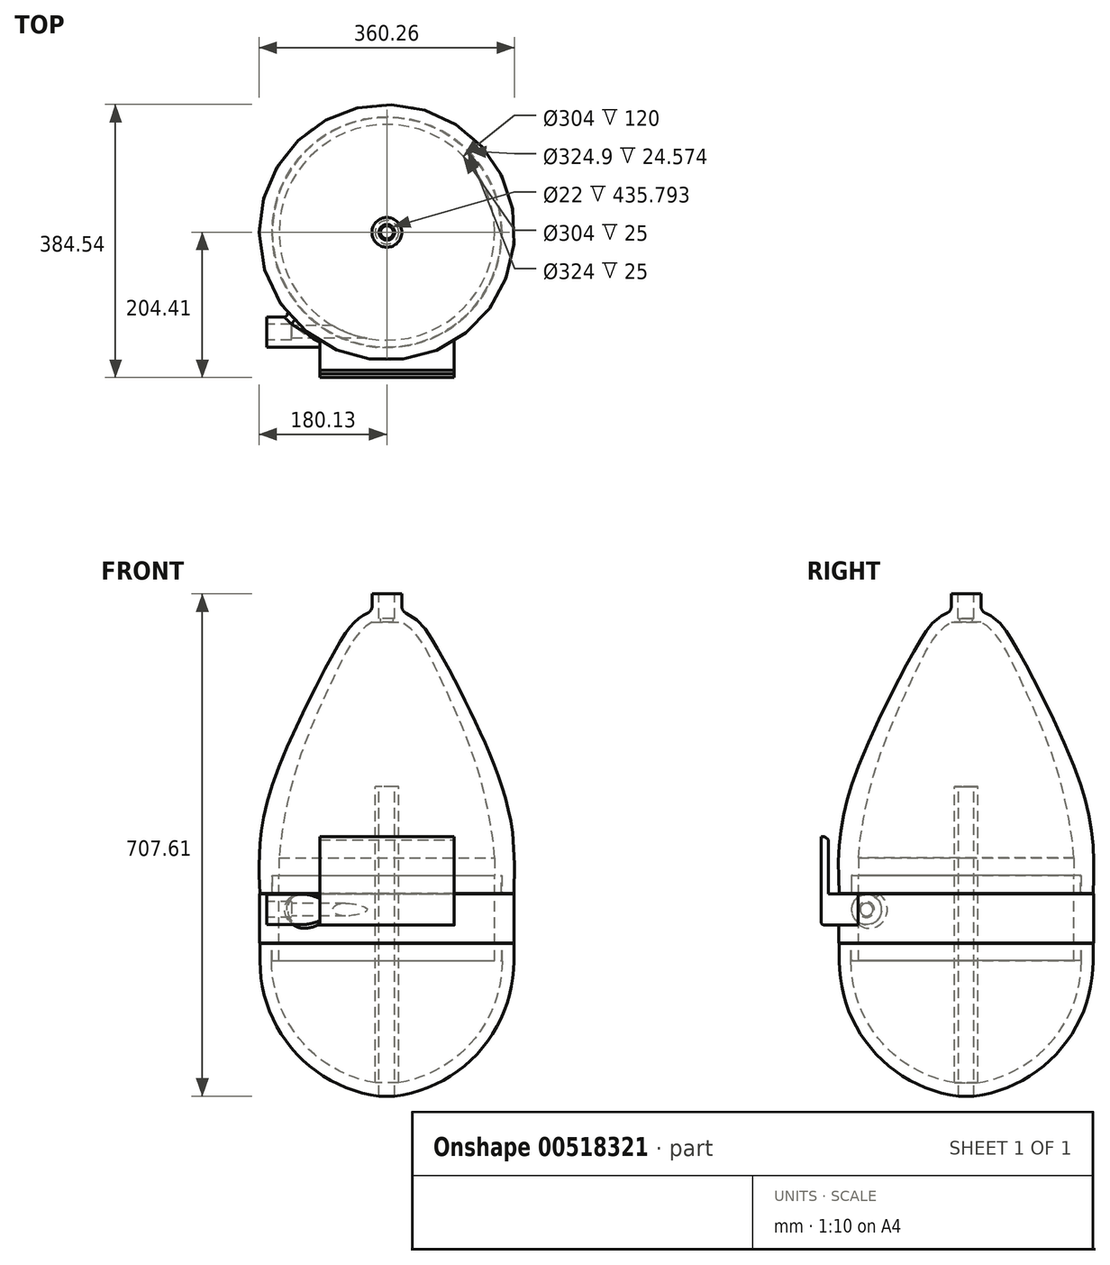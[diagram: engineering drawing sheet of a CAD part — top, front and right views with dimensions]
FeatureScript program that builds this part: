
annotation { "Feature Type Name" : "Feature", "Feature Type Description" : "" }
export const myFeature = defineFeature(function(context is Context, id is Id, definition is map)
    precondition{}
    {
        {
            var Q0;
            Q0=qCreatedBy(makeId("Front.planeOp"),FACE);
            var sketch = newSketch(context, id + "F0", { "sketchPlane" : qUnion([Q0])});
            skLineSegment(sketch, "E0", {"start": v(0, 331.82) * mm, "end": v(21, 331.82) * mm});
            skPoint(sketch, "E1", {"position": v(152, 0) * mm});
            skFitSpline(sketch, "E2", {"points": [v(21, 331.82) * mm, v(45.96, 308.45) * mm, v(72.3, 259.9) * mm, v(103.82, 190.2) * mm, v(132.28, 109.63) * mm, v(152, 0) * mm], "startDerivative": vector(216.06, -113.53) * mm, "endDerivative": vector(26.34, -404.99) * mm});
            skLineSegment(sketch, "E3", {"start": v(152, 0) * mm, "end": v(152, -50) * mm});
            skLineSegment(sketch, "E4", {"start": v(0, 0) * mm, "end": v(0, 359.59) * mm});
            skPoint(sketch, "E5", {"position": v(0, 346.82) * mm});
            skPoint(sketch, "E6", {"position": v(21, 346.82) * mm});
            skLineSegment(sketch, "E7", {"start": v(0, 346.82) * mm, "end": v(21, 346.82) * mm});
            skLineSegment(sketch, "E8", {"start": v(0, 346.82) * mm, "end": v(0, 331.82) * mm});
            skFitSpline(sketch, "E9", {"points": [v(21, 346.82) * mm, v(31.07, 342.93) * mm, v(45.96, 331.82) * mm, v(65.29, 305.23) * mm, v(159, 109.63) * mm, v(179.94, 0) * mm, v(179.02, -50) * mm], "startDerivative": vector(130.74, -24.6) * mm, "endDerivative": vector(-14.62, -301.81) * mm});
            skLineSegment(sketch, "E10", {"start": v(179.02, -50) * mm, "end": v(152, -50) * mm});
            skPoint(sketch, "E11", {"position": v(55.32, 293.43) * mm});
            skSolve(sketch);
        }
        {
            var Q0;
            Q0=makeQuery(id+"F0.imprint","IMPRINT",FACE,{"disambiguationData":[TD([[makeQuery(id+"F0.imprint","IMPRINT",EDGE,{"derivedFrom":sQuery(id+"F0.wireOp",EDGE,"E0")}),1.0]])]});
            var Q1;
            Q1=sQuery(id+"F0.wireOp",EDGE,"E4");
            revolve(context, id + "F1", {"entities" : qUnion([Q0]), "axis" : qUnion([Q1]), "revolveType" : RevolveType.FULL});
        }
        {
            var Q0;
            Q0=makeQuery(id+"F1.opRevolve","SWEPT_FACE",FACE,{"disambiguationData":[OSD([sQuery(id+"F0.wireOp",EDGE,"E7")])]});
            var sketch = newSketch(context, id + "F2", { "sketchPlane" : qUnion([Q0])});
            skCircle(sketch, "E12", {"center": v(0, 0) * mm, "radius": 9 * mm});
            skSolve(sketch);
        }
        {
            var Q0;
            Q0 = qSketchRegion(id + "F2", true);
            extrude(context, id + "F3", {"entities" : qUnion([Q0]), "operationType" : NewBodyOperationType.REMOVE, "oppositeDirection" : true, "depth" : 17 * mm, "offsetDistance" : 25 * mm});
        }
        {
            var Q0;
            Q0=makeQuery(id+"F1.opRevolve","SWEPT_FACE",FACE,{"disambiguationData":[OSD([sQuery(id+"F0.wireOp",EDGE,"E7")])]});
            var sketch = newSketch(context, id + "F4", { "sketchPlane" : qUnion([Q0])});
            skCircle(sketch, "E13", {"center": v(0, 0) * mm, "radius": 11.1 * mm});
            skSolve(sketch);
        }
        {
            var Q0;
            Q0 = qSketchRegion(id + "F4", true);
            extrude(context, id + "F5", {"entities" : qUnion([Q0]), "operationType" : NewBodyOperationType.REMOVE, "oppositeDirection" : true, "depth" : 10 * mm, "offsetDistance" : 25 * mm});
        }
        {
            var Q0;
            Q0=makeQuery(id+"F1.opRevolve","SWEPT_FACE",FACE,{"disambiguationData":[OSD([sQuery(id+"F0.wireOp",EDGE,"E7")])]});
            var sketch = newSketch(context, id + "F6", { "sketchPlane" : qUnion([Q0])});
            skCircle(sketch, "E14", {"center": v(0, 0) * mm, "radius": 21 * mm});
            skPoint(sketch, "E14.first.point", {"position": v(-12.3, 17.02) * mm});
            skPoint(sketch, "E14.second.point", {"position": v(20.38, 5.06) * mm});
            skPoint(sketch, "E14.third.point", {"position": v(-6.2, -20.06) * mm});
            skCircle(sketch, "E15", {"center": v(0, 0) * mm, "radius": 11.1 * mm});
            skPoint(sketch, "E15.first.point", {"position": v(-5.48, 9.65) * mm});
            skPoint(sketch, "E15.second.point", {"position": v(10.92, 2) * mm});
            skPoint(sketch, "E15.third.point", {"position": v(-2.11, -10.9) * mm});
            skSolve(sketch);
        }
        {
            var Q0;
            Q0 = qSketchRegion(id + "F6", true);
            extrude(context, id + "F7", {"entities" : qUnion([Q0]), "operationType" : NewBodyOperationType.ADD, "depth" : 25 * mm, "offsetDistance" : 25 * mm});
        }
        {
            var Q0;
            Q0=makeQuery(id+"F7.boolean.opBoolean","MERGE",EDGE,{"derivedFrom":[makeQuery(id+"F1.opRevolve","SWEPT_EDGE",EDGE,{"disambiguationData":[OSD([sQuery(id+"F0.wireOp",EDGE,"E7"),sQuery(id+"F0.wireOp",EDGE,"E9")])]}),makeQuery(id+"F7.opExtrude","CAP_EDGE",EDGE,{"disambiguationData":[OSD([sQuery(id+"F6.wireOp",EDGE,"E14")])],"isStart":true})]});
            fillet(context, id + "F8", {"entities" : qUnion([Q0]), "radius" : 10 * mm, "tangentPropagation" : true, "allowEdgeOverflow" : false});
        }
        {
            var Q0;
            Q0=makeQuery(id+"F1.opRevolve","SWEPT_FACE",FACE,{"disambiguationData":[OSD([sQuery(id+"F0.wireOp",EDGE,"E10")])]});
            var sketch = newSketch(context, id + "F9", { "sketchPlane" : qUnion([Q0])});
            skCircle(sketch, "E16", {"center": v(0, 0) * mm, "radius": 152 * mm});
            skPoint(sketch, "E16.first.point", {"position": v(90.88, 121.84) * mm});
            skPoint(sketch, "E16.second.point", {"position": v(-140.93, -56.95) * mm});
            skPoint(sketch, "E16.third.point", {"position": v(89.1, -123.15) * mm});
            skCircle(sketch, "E17", {"center": v(0, 0) * mm, "radius": 162 * mm});
            skSolve(sketch);
        }
        {
            var Q0;
            Q0 = qSketchRegion(id + "F9", true);
            extrude(context, id + "F10", {"entities" : qUnion([Q0]), "operationType" : NewBodyOperationType.REMOVE, "oppositeDirection" : true, "depth" : 25 * mm, "offsetDistance" : 25 * mm});
        }
        {
            var Q0;
            Q0=makeQuery(id+"F10.boolean.opBoolean","COPY",FACE,{"derivedFrom":makeQuery(id+"F10.opExtrude","CAP_FACE",FACE,{"disambiguationData":[OSD([sQuery(id+"F9.wireOp",EDGE,"E16"),sQuery(id+"F9.wireOp",EDGE,"E17")])],"isStart":false})});
            var sketch = newSketch(context, id + "F11", { "sketchPlane" : qUnion([Q0])});
            skCircle(sketch, "E18", {"center": v(0, 0) * mm, "radius": 152 * mm});
            skPoint(sketch, "E18.first.point", {"position": v(118.86, -94.74) * mm});
            skPoint(sketch, "E18.second.point", {"position": v(-147.64, -36.14) * mm});
            skPoint(sketch, "E18.third.point", {"position": v(31.37, 148.73) * mm});
            skCircle(sketch, "E19", {"center": v(0, 0) * mm, "radius": 161.5 * mm});
            skSolve(sketch);
        }
        {
            var Q0;
            Q0 = qSketchRegion(id + "F11", true);
            extrude(context, id + "F12", {"entities" : qUnion([Q0]), "depth" : 26 * mm, "offsetDistance" : 25 * mm});
        }
        {
            var Q0;
            Q0=makeQuery(id+"F12.opExtrude","CAP_FACE",FACE,{"disambiguationData":[OSD([sQuery(id+"F11.wireOp",EDGE,"E18"),sQuery(id+"F11.wireOp",EDGE,"E19")])],"isStart":false});
            var sketch = newSketch(context, id + "F13", { "sketchPlane" : qUnion([Q0])});
            skCircle(sketch, "E20", {"center": v(0, 0) * mm, "radius": 152 * mm});
            skPoint(sketch, "E20.first.point", {"position": v(152, 0) * mm});
            skPoint(sketch, "E20.second.point", {"position": v(-49.02, -143.88) * mm});
            skPoint(sketch, "E20.third.point", {"position": v(-36.04, 147.67) * mm});
            skCircle(sketch, "E21", {"center": v(0, 0) * mm, "radius": 179.5 * mm});
            skSolve(sketch);
        }
        {
            var Q0;
            Q0 = qSketchRegion(id + "F13", true);
            extrude(context, id + "F14", {"entities" : qUnion([Q0]), "operationType" : NewBodyOperationType.ADD, "depth" : 44 * mm, "offsetDistance" : 25 * mm});
        }
        {
            var Q0;
            Q0=makeQuery(id+"F14.opExtrude","CAP_FACE",FACE,{"disambiguationData":[OSD([sQuery(id+"F13.wireOp",EDGE,"E20"),sQuery(id+"F13.wireOp",EDGE,"E21")])],"isStart":false});
            var sketch = newSketch(context, id + "F15", { "sketchPlane" : qUnion([Q0])});
            skLineSegment(sketch, "E22.bottom", {"start": v(95.04, 152.28) * mm, "end": v(-94.69, 152.28) * mm});
            skLineSegment(sketch, "E22.top", {"start": v(95.04, 194.41) * mm, "end": v(-94.69, 194.41) * mm});
            skLineSegment(sketch, "E22.left", {"start": v(95.04, 152.28) * mm, "end": v(95.04, 194.41) * mm});
            skLineSegment(sketch, "E22.right", {"start": v(-94.69, 152.28) * mm, "end": v(-94.69, 194.41) * mm});
            skSolve(sketch);
        }
        {
            var Q0;
            Q0 = qSketchRegion(id + "F15", true);
            extrude(context, id + "F16", {"entities" : qUnion([Q0]), "operationType" : NewBodyOperationType.ADD, "oppositeDirection" : true, "depth" : 44 * mm, "offsetDistance" : 25 * mm});
        }
        {
            var Q0;
            Q0=makeQuery(id+"F16.opExtrude","SWEPT_FACE",FACE,{"disambiguationData":[OSD([sQuery(id+"F15.wireOp",EDGE,"E22.right")])]});
            var sketch = newSketch(context, id + "F17", { "sketchPlane" : qUnion([Q0])});
            skCircle(sketch, "E23", {"center": v(140.5, -73) * mm, "radius": 21.27 * mm});
            skPoint(sketch, "E23.centerSnap0", {"position": v(152.5, -73) * mm});
            skSolve(sketch);
        }
        {
            var Q0;
            Q0 = qSketchRegion(id + "F17", true);
            extrude(context, id + "F18", {"entities" : qUnion([Q0]), "operationType" : NewBodyOperationType.ADD, "depth" : 75 * mm, "offsetDistance" : 25 * mm});
        }
        {
            var Q0;
            Q0=makeQuery(id+"F18.opExtrude","CAP_FACE",FACE,{"disambiguationData":[OSD([sQuery(id+"F17.wireOp",EDGE,"E23")])],"isStart":false});
            var sketch = newSketch(context, id + "F19", { "sketchPlane" : qUnion([Q0])});
            skCircle(sketch, "E24", {"center": v(140.5, -73) * mm, "radius": 9 * mm});
            skSolve(sketch);
        }
        {
            var Q0;
            Q0 = qSketchRegion(id + "F19", true);
            extrude(context, id + "F20", {"entities" : qUnion([Q0]), "operationType" : NewBodyOperationType.REMOVE, "oppositeDirection" : true, "depth" : 143 * mm, "offsetDistance" : 25 * mm});
        }
        {
            var Q0;
            Q0=makeQuery(id+"F16.boolean.opBoolean","MERGE",FACE,{"derivedFrom":[makeQuery(id+"F14.opExtrude","CAP_FACE",FACE,{"disambiguationData":[OSD([sQuery(id+"F13.wireOp",EDGE,"E20"),sQuery(id+"F13.wireOp",EDGE,"E21")])],"isStart":false}),makeQuery(id+"F16.opExtrude","CAP_FACE",FACE,{"disambiguationData":[OSD([sQuery(id+"F15.wireOp",EDGE,"E22.bottom"),sQuery(id+"F15.wireOp",EDGE,"E22.top"),sQuery(id+"F15.wireOp",EDGE,"E22.left"),sQuery(id+"F15.wireOp",EDGE,"E22.right")])],"isStart":true})]});
            var sketch = newSketch(context, id + "F21", { "sketchPlane" : qUnion([Q0])});
            skCircle(sketch, "E25", {"center": v(0, 0) * mm, "radius": 152 * mm});
            skPoint(sketch, "E25.first.point", {"position": v(105.1, 109.8) * mm});
            skPoint(sketch, "E25.second.point", {"position": v(-35.54, -147.79) * mm});
            skPoint(sketch, "E25.third.point", {"position": v(-116.2, 97.98) * mm});
            skCircle(sketch, "E26", {"center": v(0, 0) * mm, "radius": 179.5 * mm});
            skPoint(sketch, "E26.first.point", {"position": v(142, 109.8) * mm});
            skPoint(sketch, "E26.second.point", {"position": v(0.2, -179.5) * mm});
            skPoint(sketch, "E26.second.point.positionSnap0", {"position": v(-0.2, -179.5) * mm});
            skPoint(sketch, "E26.third.point", {"position": v(-173.72, 45.18) * mm});
            skSolve(sketch);
        }
        {
            var Q0;
            Q0 = qSketchRegion(id + "F21", true);
            extrude(context, id + "F22", {"entities" : qUnion([Q0]), "operationType" : NewBodyOperationType.ADD, "depth" : 25 * mm, "offsetDistance" : 25 * mm});
        }
        {
            var Q0;
            Q0=makeQuery(id+"F16.opExtrude","SWEPT_FACE",FACE,{"disambiguationData":[OSD([sQuery(id+"F15.wireOp",EDGE,"E22.top")])]});
            var sketch = newSketch(context, id + "F23", { "sketchPlane" : qUnion([Q0])});
            skLineSegment(sketch, "E27.bottom", {"start": v(95.04, -95) * mm, "end": v(-94.69, -95) * mm});
            skLineSegment(sketch, "E27.top", {"start": v(95.04, 55) * mm, "end": v(-94.69, 55) * mm});
            skLineSegment(sketch, "E27.left", {"start": v(95.04, -95) * mm, "end": v(95.04, 55) * mm});
            skLineSegment(sketch, "E27.right", {"start": v(-94.69, -95) * mm, "end": v(-94.69, 55) * mm});
            skSolve(sketch);
        }
        {
            var Q0;
            Q0 = qSketchRegion(id + "F23", true);
            extrude(context, id + "F24", {"entities" : qUnion([Q0]), "operationType" : NewBodyOperationType.ADD, "depth" : 10 * mm, "offsetDistance" : 25 * mm});
        }
        {
            var Q0;
            Q0=makeQuery(id+"F24.opExtrude","CAP_FACE",FACE,{"disambiguationData":[OSD([sQuery(id+"F23.wireOp",EDGE,"E27.bottom"),sQuery(id+"F23.wireOp",EDGE,"E27.top"),sQuery(id+"F23.wireOp",EDGE,"E27.left"),sQuery(id+"F23.wireOp",EDGE,"E27.right")])],"isStart":false});
            var sketch = newSketch(context, id + "F25", { "sketchPlane" : qUnion([Q0])});
            skLineSegment(sketch, "E28.bottom", {"start": v(-94.69, 55) * mm, "end": v(95.04, 55) * mm});
            skLineSegment(sketch, "E28.top", {"start": v(-94.69, 30) * mm, "end": v(95.04, 30) * mm});
            skLineSegment(sketch, "E28.left", {"start": v(-94.69, 55) * mm, "end": v(-94.69, 30) * mm});
            skLineSegment(sketch, "E28.right", {"start": v(95.04, 55) * mm, "end": v(95.04, 30) * mm});
            skSolve(sketch);
        }
        {
            var Q0;
            Q0 = qSketchRegion(id + "F25", true);
            extrude(context, id + "F26", {"entities" : qUnion([Q0]), "operationType" : NewBodyOperationType.REMOVE, "oppositeDirection" : true, "depth" : 15 * mm, "offsetDistance" : 25 * mm});
        }
        {
            var Q0;
            Q0=makeQuery(id+"F24.opExtrude","CAP_EDGE",EDGE,{"disambiguationData":[OSD([sQuery(id+"F23.wireOp",EDGE,"E27.bottom")])],"isStart":false});
            fillet(context, id + "F27", {"entities" : qUnion([Q0]), "radius" : 5 * mm, "tangentPropagation" : true, "allowEdgeOverflow" : false});
        }
        {
            var Q0;
            Q0=makeQuery(id+"F22.opExtrude","CAP_FACE",FACE,{"disambiguationData":[OSD([sQuery(id+"F21.wireOp",EDGE,"E25"),sQuery(id+"F21.wireOp",EDGE,"E26")])],"isStart":false});
            var sketch = newSketch(context, id + "F28", { "sketchPlane" : qUnion([Q0])});
            skCircle(sketch, "E29", {"center": v(0, 0) * mm, "radius": 152 * mm});
            skPoint(sketch, "E29.first.point", {"position": v(-42.08, 146.06) * mm});
            skPoint(sketch, "E29.second.point", {"position": v(144.39, -47.5) * mm});
            skPoint(sketch, "E29.third.point", {"position": v(-99.24, -115.13) * mm});
            skCircle(sketch, "E30", {"center": v(0, 0) * mm, "radius": 162 * mm});
            skSolve(sketch);
        }
        {
            var Q0;
            Q0 = qSketchRegion(id + "F28", true);
            extrude(context, id + "F29", {"entities" : qUnion([Q0]), "operationType" : NewBodyOperationType.ADD, "depth" : 25 * mm, "offsetDistance" : 25 * mm});
        }
        {
            var Q0;
            Q0=qCreatedBy(makeId("Right.planeOp"),FACE);
            var sketch = newSketch(context, id + "F30", { "sketchPlane" : qUnion([Q0])});
            skLineSegment(sketch, "E31", {"start": v(-162.45, -120.8) * mm, "end": v(-162.45, -145.37) * mm});
            skLineSegment(sketch, "E32", {"start": v(-162.45, -120.8) * mm, "end": v(-178.93, -120.8) * mm});
            skLineSegment(sketch, "E33", {"start": v(-178.93, -120.8) * mm, "end": v(-178.93, -145.37) * mm});
            skArc(sketch, "E34", {"start": v(-162.45, -145.37) * mm, "mid": v(-115.5, -264.21) * mm, "end": v(0, -318.87) * mm});
            skArc(sketch, "E35", {"start": v(-178.93, -145.37) * mm, "mid": v(-127.24, -276.41) * mm, "end": v(0, -336.86) * mm});
            skLineSegment(sketch, "E36", {"start": v(0, -336.86) * mm, "end": v(0, -318.87) * mm});
            skLineSegment(sketch, "E37", {"start": v(0, -154.91) * mm, "end": v(0, -349.77) * mm});
            skSolve(sketch);
        }
        {
            var Q0;
            Q0=makeQuery(id+"F30.imprint","IMPRINT",FACE,{"disambiguationData":[TD([[makeQuery(id+"F30.imprint","IMPRINT",EDGE,{"derivedFrom":sQuery(id+"F30.wireOp",EDGE,"E31")}),-1.0]])]});
            var Q1;
            Q1=sQuery(id+"F30.wireOp",EDGE,"E37");
            revolve(context, id + "F31", {"entities" : qUnion([Q0]), "axis" : qUnion([Q1]), "revolveType" : RevolveType.FULL});
        }
        {
            var Q0;
            Q0=qCreatedBy(makeId("Top.planeOp"),FACE);
            var sketch = newSketch(context, id + "F32", { "sketchPlane" : qUnion([Q0])});
            skCircle(sketch, "E38", {"center": v(0, 0) * mm, "radius": 16.5 * mm});
            skCircle(sketch, "E39", {"center": v(0, 0) * mm, "radius": 11 * mm});
            skSolve(sketch);
        }
        {
            var Q0;
            Q0 = qSketchRegion(id + "F32", true);
            extrude(context, id + "F33", {"entities" : qUnion([Q0]), "operationType" : NewBodyOperationType.ADD, "oppositeDirection" : true, "depth" : 335 * mm, "offsetDistance" : 25 * mm});
        }
        {
            var Q0;
            Q0=qCreatedBy(makeId("Top.planeOp"),FACE);
            var sketch = newSketch(context, id + "F34", { "sketchPlane" : qUnion([Q0])});
            skCircle(sketch, "E40", {"center": v(0, 0) * mm, "radius": 11 * mm});
            skSolve(sketch);
        }
        {
            var Q0;
            Q0 = qSketchRegion(id + "F34", true);
            extrude(context, id + "F35", {"entities" : qUnion([Q0]), "operationType" : NewBodyOperationType.REMOVE, "oppositeDirection" : true, "depth" : 338.6 * mm, "offsetDistance" : 25 * mm});
        }
        {
            var Q0;
            Q0=makeQuery(id+"F16.opExtrude","SWEPT_EDGE",EDGE,{"disambiguationData":[OSD([sQuery(id+"F13.wireOp",EDGE,"E21"),sQuery(id+"F15.wireOp",EDGE,"E22.bottom"),sQuery(id+"F15.wireOp",EDGE,"E22.left")])]});
            var Q1;
            {var subQ0=sQuery(id+"F15.wireOp",EDGE,"E22.right");var subQ1=makeQuery(id+"F16.opExtrude","SWEPT_FACE",FACE,{"disambiguationData":[OSD([subQ0])]});var subQ2=sQuery(id+"F13.wireOp",EDGE,"E21");var subQ3=makeQuery(id+"F14.opExtrude","SWEPT_FACE",FACE,{"disambiguationData":[OSD([subQ2])]});Q1=makeQuery(id+"F18.boolean.opBoolean","SPLIT",EDGE,{"disambiguationData":[TD([makeQuery(id+"F14.opExtrude","CAP_FACE",FACE,{"disambiguationData":[OSD([sQuery(id+"F13.wireOp",EDGE,"E20"),subQ2])],"isStart":false})])],"derivedFrom":makeQuery(id+"F16.boolean.opBoolean","INTERSECT",EDGE,{"derivedFrom":[subQ3,subQ1]})});}
            var Q2;
            Q2=makeQuery(id+"F18.boolean.opBoolean","INTERSECT",EDGE,{"derivedFrom":[makeQuery(id+"F14.opExtrude","SWEPT_FACE",FACE,{"disambiguationData":[OSD([sQuery(id+"F13.wireOp",EDGE,"E21")])]}),makeQuery(id+"F18.opExtrude","SWEPT_FACE",FACE,{"disambiguationData":[OSD([sQuery(id+"F17.wireOp",EDGE,"E23")])]})]});
            var Q3;
            Q3=makeQuery(id+"F18.opExtrude","CAP_EDGE",EDGE,{"disambiguationData":[OSD([sQuery(id+"F17.wireOp",EDGE,"E23")])],"isStart":true});
            var Q4;
            Q4=makeQuery(id+"F22.opExtrude","CAP_EDGE",EDGE,{"disambiguationData":[OSD([sQuery(id+"F21.wireOp",EDGE,"E26")])],"isStart":true});
            fillet(context, id + "F36", {"entities" : qUnion([Q0, Q1, Q2, Q3, Q4]), "radius" : 5 * mm, "tangentPropagation" : true, "allowEdgeOverflow" : false});
        }
        {
            var Q0;
            Q0=makeQuery(id+"F33.opExtrude","CAP_FACE",FACE,{"disambiguationData":[OSD([sQuery(id+"F32.wireOp",EDGE,"E38"),sQuery(id+"F32.wireOp",EDGE,"E39")])],"isStart":true});
            var sketch = newSketch(context, id + "F37", { "sketchPlane" : qUnion([Q0])});
            skCircle(sketch, "E41", {"center": v(0, 0) * mm, "radius": 11 * mm});
            skPoint(sketch, "E41.first.point", {"position": v(2.37, -10.74) * mm});
            skPoint(sketch, "E41.second.point", {"position": v(-9.82, 4.96) * mm});
            skPoint(sketch, "E41.third.point", {"position": v(8.52, 6.96) * mm});
            skCircle(sketch, "E42", {"center": v(0, 0) * mm, "radius": 16.5 * mm});
            skPoint(sketch, "E42.first.point", {"position": v(-9.98, -13.14) * mm});
            skPoint(sketch, "E42.second.point", {"position": v(15.35, -6.06) * mm});
            skPoint(sketch, "E42.third.point", {"position": v(-9.77, 13.3) * mm});
            skSolve(sketch);
        }
        {
            var Q0;
            Q0 = qSketchRegion(id + "F37", true);
            extrude(context, id + "F38", {"entities" : qUnion([Q0]), "operationType" : NewBodyOperationType.ADD, "depth" : 100 * mm, "offsetDistance" : 25 * mm});
        }
        {
            var Q0;
            Q0=makeQuery(id+"F26.boolean.opBoolean","COPY",EDGE,{"derivedFrom":makeQuery(id+"F26.opExtrude","SWEPT_EDGE",EDGE,{"disambiguationData":[OSD([sQuery(id+"F23.wireOp",EDGE,"E27.left"),sQuery(id+"F25.wireOp",EDGE,"E28.top"),sQuery(id+"F25.wireOp",EDGE,"E28.right")])]})});
            var Q1;
            Q1=makeQuery(id+"F26.boolean.opBoolean","INTERSECT",EDGE,{"derivedFrom":[makeQuery(id+"F24.opExtrude","CAP_FACE",FACE,{"disambiguationData":[OSD([sQuery(id+"F23.wireOp",EDGE,"E27.bottom"),sQuery(id+"F23.wireOp",EDGE,"E27.top"),sQuery(id+"F23.wireOp",EDGE,"E27.left"),sQuery(id+"F23.wireOp",EDGE,"E27.right")])],"isStart":true}),makeQuery(id+"F26.opExtrude","SWEPT_FACE",FACE,{"disambiguationData":[OSD([sQuery(id+"F25.wireOp",EDGE,"E28.top")])]})]});
            var Q2;
            Q2=makeQuery(id+"F26.boolean.opBoolean","COPY",EDGE,{"derivedFrom":makeQuery(id+"F26.opExtrude","SWEPT_EDGE",EDGE,{"disambiguationData":[OSD([sQuery(id+"F23.wireOp",EDGE,"E27.right"),sQuery(id+"F25.wireOp",EDGE,"E28.top"),sQuery(id+"F25.wireOp",EDGE,"E28.left")])]})});
            chamfer(context, id + "F39", {"entities" : qUnion([Q0, Q1, Q2]), "width" : 5 * mm, "tangentPropagation" : true});
        }
        {
            var Q0;
            Q0=makeQuery(id+"F18.opExtrude","CAP_FACE",FACE,{"disambiguationData":[OSD([sQuery(id+"F17.wireOp",EDGE,"E23")])],"isStart":false});
            var sketch = newSketch(context, id + "F40", { "sketchPlane" : qUnion([Q0])});
            skCircle(sketch, "E43", {"center": v(140.5, -73) * mm, "radius": 11.1 * mm});
            skSolve(sketch);
        }
        {
            var Q0;
            Q0 = qSketchRegion(id + "F40", true);
            extrude(context, id + "F41", {"entities" : qUnion([Q0]), "operationType" : NewBodyOperationType.REMOVE, "oppositeDirection" : true, "depth" : 35 * mm, "offsetDistance" : 25 * mm});
        }
    });
